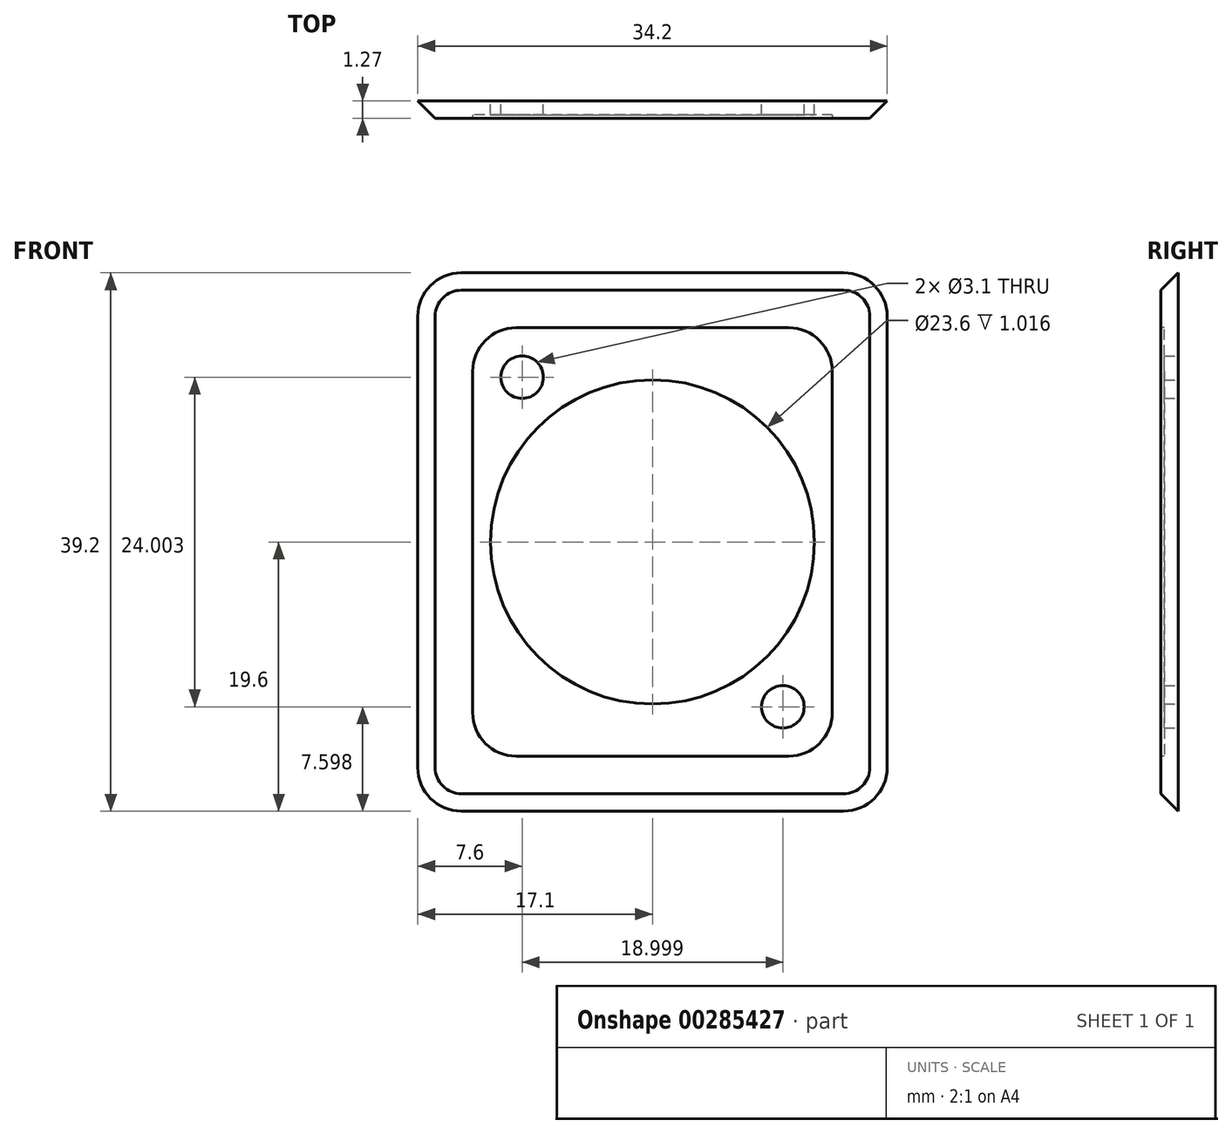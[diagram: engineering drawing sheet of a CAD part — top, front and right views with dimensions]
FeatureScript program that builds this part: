
annotation { "Feature Type Name" : "Feature", "Feature Type Description" : "" }
export const myFeature = defineFeature(function(context is Context, id is Id, definition is map)
    precondition{}
    {
        {
            var Q0;
            Q0=qCreatedBy(makeId("Front.planeOp"),FACE);
            var sketch = newSketch(context, id + "F0", { "sketchPlane" : qUnion([Q0])});
            skLineSegment(sketch, "E0.bottom", {"start": v(3.18, 0) * mm, "end": v(31.02, 0) * mm});
            skLineSegment(sketch, "E0.top", {"start": v(3.17, 39.2) * mm, "end": v(31.02, 39.2) * mm});
            skLineSegment(sketch, "E0.left", {"start": v(0, 3.18) * mm, "end": v(0, 36.02) * mm});
            skLineSegment(sketch, "E0.right", {"start": v(34.2, 3.18) * mm, "end": v(34.2, 36.02) * mm});
            skCircle(sketch, "E1", {"center": v(17.1, 19.6) * mm, "radius": 11.8 * mm});
            skLineSegment(sketch, "E2", {"start": v(17.1, 39.2) * mm, "end": v(17.1, 0) * mm, "construction": true});
            skLineSegment(sketch, "E3", {"start": v(34.2, 19.6) * mm, "end": v(0, 19.6) * mm, "construction": true});
            skCircle(sketch, "E4", {"center": v(7.6, 31.6) * mm, "radius": 1.55 * mm});
            skCircle(sketch, "E5", {"center": v(26.6, 7.6) * mm, "radius": 1.55 * mm});
            skPoint(sketch, "E6.visualSharp", {"position": v(0, 39.2) * mm});
            skArc(sketch, "E6.filletArc", {"start": v(3.17, 39.2) * mm, "mid": v(0.93, 38.27) * mm, "end": v(0, 36.02) * mm});
            skPoint(sketch, "E7.visualSharp", {"position": v(34.2, 39.2) * mm});
            skArc(sketch, "E7.filletArc", {"start": v(34.2, 36.02) * mm, "mid": v(33.27, 38.27) * mm, "end": v(31.02, 39.2) * mm});
            skPoint(sketch, "E8.visualSharp", {"position": v(34.2, 0) * mm});
            skArc(sketch, "E8.filletArc", {"start": v(31.02, 0) * mm, "mid": v(33.27, 0.93) * mm, "end": v(34.2, 3.18) * mm});
            skPoint(sketch, "E9.visualSharp", {"position": v(0, 0) * mm});
            skArc(sketch, "E9.filletArc", {"start": v(0, 3.17) * mm, "mid": v(0.93, 0.93) * mm, "end": v(3.18, 0) * mm});
            skSolve(sketch);
        }
        {
            var Q0;
            Q0=qSketchRegion(id+"F0",true);
            extrude(context, id + "F1", {"entities" : qUnion([Q0]), "depth" : 1.27 * mm});
        }
        {
            var Q0;
            Q0=makeQuery(id+"F1.opExtrude","CAP_FACE",FACE,{"disambiguationData":[OSD([sQuery(id+"F0.wireOp",EDGE,"E0.bottom"),sQuery(id+"F0.wireOp",EDGE,"E0.top"),sQuery(id+"F0.wireOp",EDGE,"E0.left"),sQuery(id+"F0.wireOp",EDGE,"E0.right"),sQuery(id+"F0.wireOp",EDGE,"E1"),sQuery(id+"F0.wireOp",EDGE,"E4"),sQuery(id+"F0.wireOp",EDGE,"E5"),sQuery(id+"F0.wireOp",EDGE,"E6.filletArc"),sQuery(id+"F0.wireOp",EDGE,"E7.filletArc"),sQuery(id+"F0.wireOp",EDGE,"E8.filletArc"),sQuery(id+"F0.wireOp",EDGE,"E9.filletArc")])],"isStart":false});
            var sketch = newSketch(context, id + "F2", { "sketchPlane" : qUnion([Q0])});
            skLineSegment(sketch, "E10.bottom", {"start": v(7.17, 35.2) * mm, "end": v(27.03, 35.2) * mm});
            skLineSegment(sketch, "E10.top", {"start": v(7.17, 4) * mm, "end": v(27.02, 4) * mm});
            skLineSegment(sketch, "E10.left", {"start": v(4, 32.02) * mm, "end": v(4, 7.18) * mm});
            skLineSegment(sketch, "E10.right", {"start": v(30.2, 32.02) * mm, "end": v(30.2, 7.17) * mm});
            skLineSegment(sketch, "E11", {"start": v(17.1, 39.2) * mm, "end": v(17.1, 4) * mm, "construction": true});
            skLineSegment(sketch, "E12", {"start": v(34.2, 19.6) * mm, "end": v(4, 19.6) * mm, "construction": true});
            skPoint(sketch, "E13.visualSharp", {"position": v(4, 35.2) * mm});
            skArc(sketch, "E13.filletArc", {"start": v(7.17, 35.2) * mm, "mid": v(4.93, 34.27) * mm, "end": v(4, 32.02) * mm});
            skPoint(sketch, "E14.visualSharp", {"position": v(30.2, 35.2) * mm});
            skArc(sketch, "E14.filletArc", {"start": v(30.2, 32.02) * mm, "mid": v(29.27, 34.27) * mm, "end": v(27.03, 35.2) * mm});
            skPoint(sketch, "E15.visualSharp", {"position": v(30.2, 4) * mm});
            skArc(sketch, "E15.filletArc", {"start": v(27.02, 4) * mm, "mid": v(29.27, 4.93) * mm, "end": v(30.2, 7.17) * mm});
            skPoint(sketch, "E16.visualSharp", {"position": v(4, 4) * mm});
            skArc(sketch, "E16.filletArc", {"start": v(4, 7.18) * mm, "mid": v(4.93, 4.93) * mm, "end": v(7.17, 4) * mm});
            skSolve(sketch);
        }
        {
            var Q0;
            Q0=qSketchRegion(id+"F2",true);
            extrude(context, id + "F3", {"entities" : qUnion([Q0]), "operationType" : NewBodyOperationType.REMOVE, "oppositeDirection" : true, "depth" : 0.25 * mm});
        }
        {
            var Q0;
            Q0=makeQuery(id+"F1.opExtrude","CAP_EDGE",EDGE,{"disambiguationData":[OSD([sQuery(id+"F0.wireOp",EDGE,"E0.right")])],"isStart":false});
            chamfer(context, id + "F4", {"entities" : qUnion([Q0]), "width" : 1.27 * mm, "tangentPropagation" : true});
        }
    });
